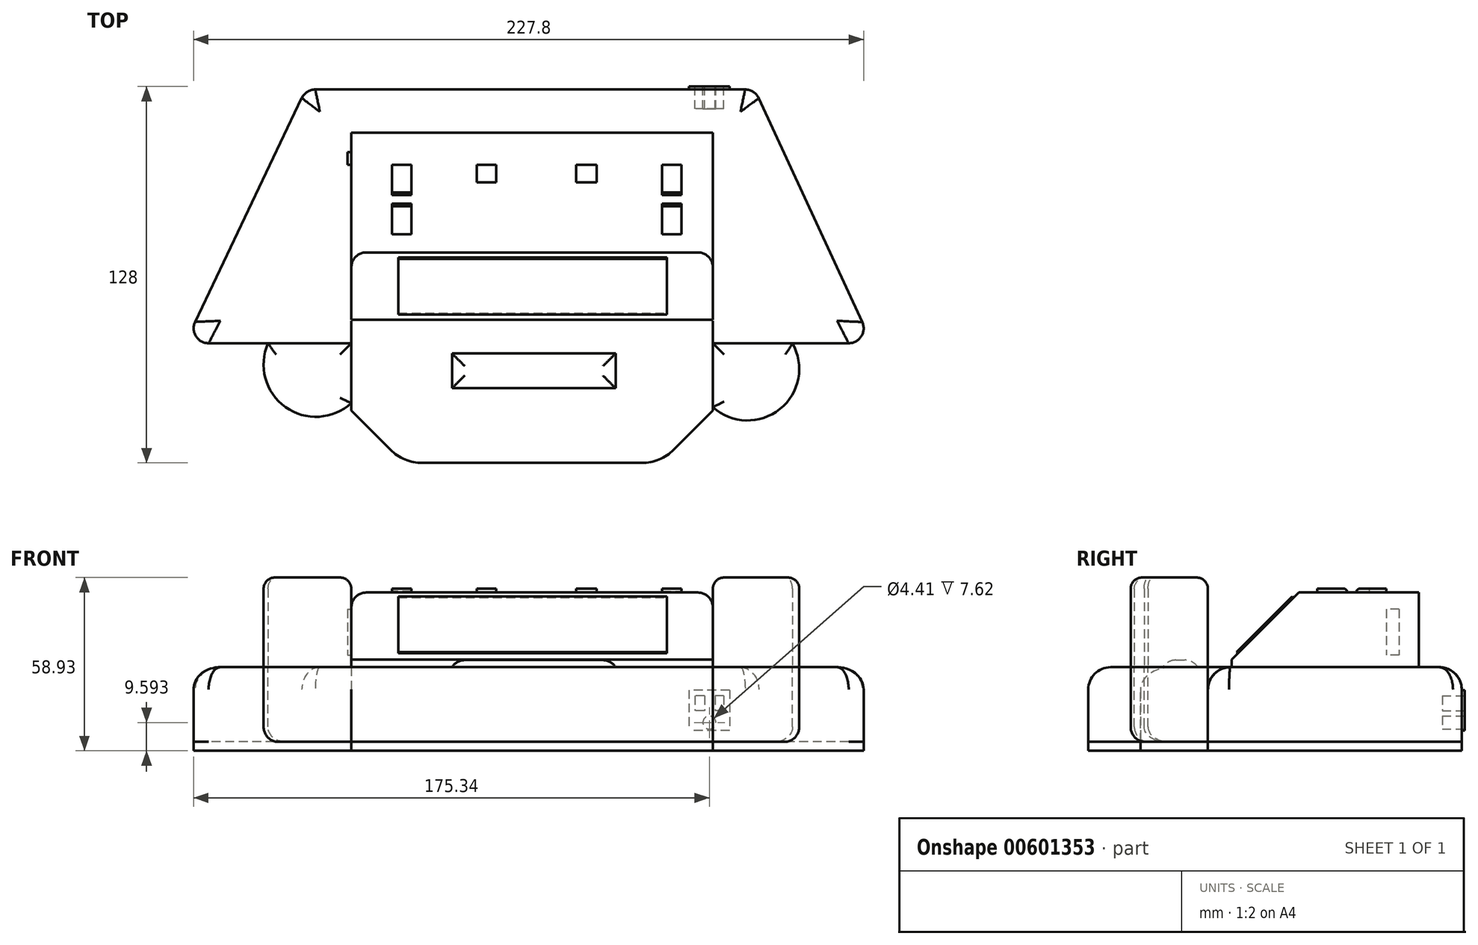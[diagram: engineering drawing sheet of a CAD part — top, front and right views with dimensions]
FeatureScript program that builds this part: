
annotation { "Feature Type Name" : "Feature", "Feature Type Description" : "" }
export const myFeature = defineFeature(function(context is Context, id is Id, definition is map)
    precondition{}
    {
        {
            var Q0;
            Q0=qCreatedBy(makeId("Top.planeOp"),FACE);
            var sketch = newSketch(context, id + "F0", { "sketchPlane" : qUnion([Q0])});
            skLineSegment(sketch, "E0", {"start": v(-105.32, 66.3) * mm, "end": v(-146.43, -19.98) * mm});
            skLineSegment(sketch, "E1", {"start": v(-146.43, -19.98) * mm, "end": v(-89.85, -19.98) * mm});
            skLineSegment(sketch, "E2", {"start": v(-89.85, -19.98) * mm, "end": v(-89.85, -60.68) * mm});
            skLineSegment(sketch, "E3", {"start": v(-89.85, -60.68) * mm, "end": v(33.07, -60.68) * mm});
            skLineSegment(sketch, "E4", {"start": v(33.07, -60.68) * mm, "end": v(33.07, -19.98) * mm});
            skLineSegment(sketch, "E5", {"start": v(33.07, -19.98) * mm, "end": v(87.2, -19.98) * mm});
            skLineSegment(sketch, "E6", {"start": v(87.2, -19.98) * mm, "end": v(47.31, 66.3) * mm});
            skLineSegment(sketch, "E7", {"start": v(47.31, 66.3) * mm, "end": v(-105.32, 66.3) * mm});
            skSolve(sketch);
        }
        {
            var Q0;
            Q0 = qSketchRegion(id + "F0", true);
            extrude(context, id + "F1", {"entities" : qUnion([Q0]), "depth" : 25.4 * mm, "offsetDistance" : 25.4 * mm});
        }
        {
            var Q0;
            Q0=makeQuery(id+"F1.opExtrude","CAP_FACE",FACE,{"disambiguationData":[OSD([sQuery(id+"F0.wireOp",EDGE,"E0"),sQuery(id+"F0.wireOp",EDGE,"E1"),sQuery(id+"F0.wireOp",EDGE,"E2"),sQuery(id+"F0.wireOp",EDGE,"E3"),sQuery(id+"F0.wireOp",EDGE,"E4"),sQuery(id+"F0.wireOp",EDGE,"E5"),sQuery(id+"F0.wireOp",EDGE,"E6"),sQuery(id+"F0.wireOp",EDGE,"E7")])],"isStart":false});
            var sketch = newSketch(context, id + "F2", { "sketchPlane" : qUnion([Q0])});
            skArc(sketch, "E8", {"start": v(-118.14, -19.98) * mm, "mid": v(-112.27, -41.66) * mm, "end": v(-89.85, -40.33) * mm});
            skArc(sketch, "E9", {"start": v(33.07, -41.66) * mm, "mid": v(55.87, -42.39) * mm, "end": v(60.13, -19.98) * mm});
            skPoint(sketch, "E9.startSnap0", {"position": v(-112.27, -41.66) * mm});
            skSolve(sketch);
        }
        {
            var Q0;
            {var subQ0=sQuery(id+"F2.wireOp",EDGE,"E9");Q0=makeQuery(id+"F2.imprint","IMPRINT",FACE,{"disambiguationData":[TD([[makeQuery(id+"F2.imprint","IMPRINT",EDGE,{"derivedFrom":subQ0}),1.0]])]});}
            var Q1;
            {var subQ0=sQuery(id+"F2.wireOp",EDGE,"E8");Q1=makeQuery(id+"F2.imprint","IMPRINT",FACE,{"disambiguationData":[TD([[makeQuery(id+"F2.imprint","IMPRINT",EDGE,{"derivedFrom":subQ0}),1.0]])]});}
            extrude(context, id + "F3", {"entities" : qUnion([Q0, Q1]), "oppositeDirection" : true, "depth" : 25.4 * mm, "offsetDistance" : 25.4 * mm});
        }
        {
            var Q0;
            Q0=makeQuery(id+"F1.opExtrude","SWEPT_EDGE",EDGE,{"disambiguationData":[OSD([sQuery(id+"F0.wireOp",EDGE,"E2"),sQuery(id+"F0.wireOp",EDGE,"E3")])]});
            var Q1;
            Q1=makeQuery(id+"F1.opExtrude","SWEPT_EDGE",EDGE,{"disambiguationData":[OSD([sQuery(id+"F0.wireOp",EDGE,"E3"),sQuery(id+"F0.wireOp",EDGE,"E4")])]});
            chamfer(context, id + "F4", {"entities" : qUnion([Q0, Q1]), "width" : 17.78 * mm, "tangentPropagation" : true});
        }
        {
            var Q0;
            Q0=makeQuery(id+"F3.opExtrude","CAP_FACE",FACE,{"disambiguationData":[OSD([sQuery(id+"F0.wireOp",EDGE,"E1"),sQuery(id+"F0.wireOp",EDGE,"E2"),sQuery(id+"F2.wireOp",EDGE,"E8")])],"isStart":true});
            var Q1;
            Q1=makeQuery(id+"F3.opExtrude","CAP_FACE",FACE,{"disambiguationData":[OSD([sQuery(id+"F0.wireOp",EDGE,"E4"),sQuery(id+"F0.wireOp",EDGE,"E5"),sQuery(id+"F2.wireOp",EDGE,"E9")])],"isStart":true});
            extrude(context, id + "F5", {"entities" : qUnion([Q0, Q1]), "depth" : 30.48 * mm, "offsetDistance" : 25.4 * mm});
        }
        {
            var Q0;
            Q0=makeQuery(id+"F1.opExtrude","CAP_FACE",FACE,{"disambiguationData":[OSD([sQuery(id+"F0.wireOp",EDGE,"E0"),sQuery(id+"F0.wireOp",EDGE,"E1"),sQuery(id+"F0.wireOp",EDGE,"E2"),sQuery(id+"F0.wireOp",EDGE,"E3"),sQuery(id+"F0.wireOp",EDGE,"E4"),sQuery(id+"F0.wireOp",EDGE,"E5"),sQuery(id+"F0.wireOp",EDGE,"E6"),sQuery(id+"F0.wireOp",EDGE,"E7")])],"isStart":false});
            var sketch = newSketch(context, id + "F6", { "sketchPlane" : qUnion([Q0])});
            skLineSegment(sketch, "E10", {"start": v(-89.85, 51.66) * mm, "end": v(33.07, 51.66) * mm});
            skLineSegment(sketch, "E11", {"start": v(33.07, 51.66) * mm, "end": v(33.07, -11.94) * mm});
            skLineSegment(sketch, "E12", {"start": v(33.07, -11.94) * mm, "end": v(-89.85, -11.94) * mm});
            skLineSegment(sketch, "E13", {"start": v(-89.85, -11.94) * mm, "end": v(-89.85, 51.66) * mm});
            skSolve(sketch);
        }
        {
            var Q0;
            Q0 = qSketchRegion(id + "F6", true);
            extrude(context, id + "F7", {"entities" : qUnion([Q0]), "depth" : 25.4 * mm, "offsetDistance" : 25.4 * mm});
        }
        {
            var Q0;
            Q0=makeQuery(id+"F7.opExtrude","CAP_EDGE",EDGE,{"disambiguationData":[OSD([sQuery(id+"F6.wireOp",EDGE,"E12")])],"isStart":false});
            chamfer(context, id + "F8", {"entities" : qUnion([Q0]), "width" : 22.86 * mm, "tangentPropagation" : true});
        }
        {
            var Q0;
            Q0=makeQuery(id+"F1.opExtrude","SWEPT_EDGE",EDGE,{"disambiguationData":[OSD([sQuery(id+"F0.wireOp",EDGE,"E0"),sQuery(id+"F0.wireOp",EDGE,"E1")])]});
            var Q1;
            Q1=makeQuery(id+"F1.opExtrude","SWEPT_EDGE",EDGE,{"disambiguationData":[OSD([sQuery(id+"F0.wireOp",EDGE,"E5"),sQuery(id+"F0.wireOp",EDGE,"E6")])]});
            var Q2;
            Q2=makeQuery(id+"F1.opExtrude","SWEPT_EDGE",EDGE,{"disambiguationData":[OSD([sQuery(id+"F0.wireOp",EDGE,"E6"),sQuery(id+"F0.wireOp",EDGE,"E7")])]});
            var Q3;
            Q3=makeQuery(id+"F1.opExtrude","SWEPT_EDGE",EDGE,{"disambiguationData":[OSD([sQuery(id+"F0.wireOp",EDGE,"E0"),sQuery(id+"F0.wireOp",EDGE,"E7")])]});
            fillet(context, id + "F9", {"entities" : qUnion([Q0, Q1, Q2, Q3]), "radius" : 5.08 * mm, "tangentPropagation" : true, "allowEdgeOverflow" : false});
        }
        {
            var Q0;
            {var subQ0=sQuery(id+"F0.wireOp",EDGE,"E3");Q0=makeQuery(id+"F4.opChamfer","BLEND_EDGE",EDGE,{"blendedFrom":[makeQuery(id+"F1.opExtrude","SWEPT_EDGE",EDGE,{"disambiguationData":[OSD([sQuery(id+"F0.wireOp",EDGE,"E2"),subQ0])]}),makeQuery(id+"F1.opExtrude","SWEPT_FACE",FACE,{"disambiguationData":[OSD([subQ0])]})],"blendedInto":[makeQuery(id+"F1.opExtrude","SWEPT_FACE",FACE,{"disambiguationData":[OSD([subQ0])]})]});}
            var Q1;
            {var subQ0=sQuery(id+"F0.wireOp",EDGE,"E3");Q1=makeQuery(id+"F4.opChamfer","BLEND_EDGE",EDGE,{"blendedFrom":[makeQuery(id+"F1.opExtrude","SWEPT_EDGE",EDGE,{"disambiguationData":[OSD([subQ0,sQuery(id+"F0.wireOp",EDGE,"E4")])]}),makeQuery(id+"F1.opExtrude","SWEPT_FACE",FACE,{"disambiguationData":[OSD([subQ0])]})],"blendedInto":[makeQuery(id+"F1.opExtrude","SWEPT_FACE",FACE,{"disambiguationData":[OSD([subQ0])]})]});}
            fillet(context, id + "F10", {"entities" : qUnion([Q0, Q1]), "radius" : 15.24 * mm, "tangentPropagation" : true, "allowEdgeOverflow" : false});
        }
        {
            var Q0;
            Q0=makeQuery(id+"F5.opExtrude","CAP_EDGE",EDGE,{"disambiguationData":[OSD([sQuery(id+"F2.wireOp",EDGE,"E8")])],"isStart":false});
            var Q1;
            Q1=makeQuery(id+"F5.opExtrude","CAP_EDGE",EDGE,{"disambiguationData":[OSD([sQuery(id+"F2.wireOp",EDGE,"E9")])],"isStart":false});
            var Q2;
            Q2=makeQuery(id+"F5.opExtrude","CAP_EDGE",EDGE,{"disambiguationData":[OSD([sQuery(id+"F0.wireOp",EDGE,"E4")])],"isStart":false});
            var Q3;
            Q3=makeQuery(id+"F5.opExtrude","CAP_EDGE",EDGE,{"disambiguationData":[OSD([sQuery(id+"F0.wireOp",EDGE,"E5")])],"isStart":false});
            var Q4;
            Q4=makeQuery(id+"F5.opExtrude","CAP_EDGE",EDGE,{"disambiguationData":[OSD([sQuery(id+"F0.wireOp",EDGE,"E2")])],"isStart":false});
            var Q5;
            Q5=makeQuery(id+"F5.opExtrude","CAP_EDGE",EDGE,{"disambiguationData":[OSD([sQuery(id+"F0.wireOp",EDGE,"E1")])],"isStart":false});
            fillet(context, id + "F11", {"entities" : qUnion([Q0, Q1, Q2, Q3, Q4, Q5]), "radius" : 3.8 * mm, "tangentPropagation" : true, "allowEdgeOverflow" : false});
        }
        {
            var Q0;
            Q0=makeQuery(id+"F1.opExtrude","CAP_FACE",FACE,{"disambiguationData":[OSD([sQuery(id+"F0.wireOp",EDGE,"E0"),sQuery(id+"F0.wireOp",EDGE,"E1"),sQuery(id+"F0.wireOp",EDGE,"E2"),sQuery(id+"F0.wireOp",EDGE,"E3"),sQuery(id+"F0.wireOp",EDGE,"E4"),sQuery(id+"F0.wireOp",EDGE,"E5"),sQuery(id+"F0.wireOp",EDGE,"E6"),sQuery(id+"F0.wireOp",EDGE,"E7")])],"isStart":true});
            var sketch = newSketch(context, id + "F12", { "sketchPlane" : qUnion([Q0])});
            skSolve(sketch);
        }
        {
            var Q0;
            {var subQ5=sQuery(id+"F0.wireOp",EDGE,"E4");Q0=makeQuery(id+"F12.imprint","IMPRINT",FACE,{"disambiguationData":[TD([[makeQuery(id+"F12.imprint","IMPRINT",EDGE,{"derivedFrom":makeQuery(id+"F1.opExtrude","CAP_EDGE",EDGE,{"disambiguationData":[OSD([subQ5])],"isStart":true})}),-1.0]])]});}
            extrude(context, id + "F13", {"entities" : qUnion([Q0]), "depth" : 3.05 * mm, "offsetDistance" : 25.4 * mm});
        }
        {
            var Q0;
            Q0=makeQuery(id+"F3.opExtrude","CAP_EDGE",EDGE,{"disambiguationData":[OSD([sQuery(id+"F2.wireOp",EDGE,"E8")])],"isStart":false});
            var Q1;
            Q1=makeQuery(id+"F3.opExtrude","CAP_EDGE",EDGE,{"disambiguationData":[OSD([sQuery(id+"F2.wireOp",EDGE,"E9")])],"isStart":false});
            fillet(context, id + "F14", {"entities" : qUnion([Q0, Q1]), "radius" : 5.08 * mm, "tangentPropagation" : true, "allowEdgeOverflow" : false});
        }
        {
            var Q0;
            Q0=makeQuery(id+"F7.opExtrude","CAP_FACE",FACE,{"disambiguationData":[OSD([sQuery(id+"F6.wireOp",EDGE,"E10"),sQuery(id+"F6.wireOp",EDGE,"E11"),sQuery(id+"F6.wireOp",EDGE,"E12"),sQuery(id+"F6.wireOp",EDGE,"E13")])],"isStart":false});
            var sketch = newSketch(context, id + "F15", { "sketchPlane" : qUnion([Q0])});
            skLineSegment(sketch, "E14", {"start": v(-6.4, 40.73) * mm, "end": v(-6.4, 34.78) * mm});
            skLineSegment(sketch, "E15", {"start": v(-6.4, 34.78) * mm, "end": v(-13.37, 34.78) * mm});
            skLineSegment(sketch, "E16", {"start": v(-13.37, 34.78) * mm, "end": v(-13.37, 40.73) * mm});
            skLineSegment(sketch, "E17", {"start": v(-13.37, 40.73) * mm, "end": v(-6.4, 40.73) * mm});
            skLineSegment(sketch, "E18", {"start": v(-47.2, 40.73) * mm, "end": v(-47.2, 34.78) * mm});
            skLineSegment(sketch, "E19", {"start": v(-47.2, 34.78) * mm, "end": v(-40.64, 34.78) * mm});
            skLineSegment(sketch, "E20", {"start": v(-40.64, 34.78) * mm, "end": v(-40.64, 40.73) * mm});
            skLineSegment(sketch, "E21", {"start": v(-40.64, 40.73) * mm, "end": v(-47.2, 40.73) * mm});
            skLineSegment(sketch, "E22.bottom", {"start": v(-76.04, 40.73) * mm, "end": v(-69.41, 40.73) * mm});
            skLineSegment(sketch, "E22.top", {"start": v(-76.04, 30.36) * mm, "end": v(-69.41, 30.36) * mm});
            skLineSegment(sketch, "E22.left", {"start": v(-76.04, 40.73) * mm, "end": v(-76.04, 30.36) * mm});
            skLineSegment(sketch, "E22.right", {"start": v(-69.41, 40.73) * mm, "end": v(-69.41, 30.36) * mm});
            skLineSegment(sketch, "E23.bottom", {"start": v(-69.41, 27.49) * mm, "end": v(-76.04, 27.49) * mm});
            skLineSegment(sketch, "E23.top", {"start": v(-69.41, 17.12) * mm, "end": v(-76.04, 17.12) * mm});
            skLineSegment(sketch, "E23.left", {"start": v(-69.41, 27.49) * mm, "end": v(-69.41, 17.12) * mm});
            skLineSegment(sketch, "E23.right", {"start": v(-76.04, 27.49) * mm, "end": v(-76.04, 17.12) * mm});
            skLineSegment(sketch, "E24.bottom", {"start": v(15.8, 40.73) * mm, "end": v(22.43, 40.73) * mm});
            skLineSegment(sketch, "E24.top", {"start": v(15.8, 30.36) * mm, "end": v(22.43, 30.36) * mm});
            skLineSegment(sketch, "E24.left", {"start": v(15.8, 40.73) * mm, "end": v(15.8, 30.36) * mm});
            skLineSegment(sketch, "E24.right", {"start": v(22.43, 40.73) * mm, "end": v(22.43, 30.36) * mm});
            skLineSegment(sketch, "E25.bottom", {"start": v(15.8, 27.5) * mm, "end": v(22.43, 27.5) * mm});
            skLineSegment(sketch, "E25.top", {"start": v(15.8, 17.12) * mm, "end": v(22.43, 17.12) * mm});
            skLineSegment(sketch, "E25.left", {"start": v(15.8, 27.5) * mm, "end": v(15.8, 17.12) * mm});
            skLineSegment(sketch, "E25.right", {"start": v(22.43, 27.5) * mm, "end": v(22.43, 17.12) * mm});
            skSolve(sketch);
        }
        {
            var Q0;
            Q0 = qSketchRegion(id + "F15", true);
            extrude(context, id + "F16", {"entities" : qUnion([Q0]), "depth" : 1.27 * mm, "offsetDistance" : 25.4 * mm});
        }
        {
            var Q0;
            Q0=makeQuery(id+"F7.opExtrude","SWEPT_FACE",FACE,{"disambiguationData":[OSD([sQuery(id+"F6.wireOp",EDGE,"E13")])]});
            var sketch = newSketch(context, id + "F17", { "sketchPlane" : qUnion([Q0])});
            skLineSegment(sketch, "E26.bottom", {"start": v(-45.04, 45.13) * mm, "end": v(-40.65, 45.13) * mm});
            skLineSegment(sketch, "E26.top", {"start": v(-45.04, 29.48) * mm, "end": v(-40.65, 29.48) * mm});
            skLineSegment(sketch, "E26.left", {"start": v(-45.04, 45.13) * mm, "end": v(-45.04, 29.48) * mm});
            skLineSegment(sketch, "E26.right", {"start": v(-40.65, 45.13) * mm, "end": v(-40.65, 29.48) * mm});
            skSolve(sketch);
        }
        {
            var Q0;
            Q0 = qSketchRegion(id + "F17", true);
            extrude(context, id + "F18", {"entities" : qUnion([Q0]), "depth" : 1.27 * mm, "offsetDistance" : 25.4 * mm});
        }
        {
            var Q0;
            Q0=makeQuery(id+"F7.opExtrude","CAP_EDGE",EDGE,{"disambiguationData":[OSD([sQuery(id+"F6.wireOp",EDGE,"E13")])],"isStart":false});
            var Q1;
            Q1=makeQuery(id+"F7.opExtrude","CAP_EDGE",EDGE,{"disambiguationData":[OSD([sQuery(id+"F6.wireOp",EDGE,"E11")])],"isStart":false});
            fillet(context, id + "F19", {"entities" : qUnion([Q0, Q1]), "radius" : 5.08 * mm, "tangentPropagation" : true, "allowEdgeOverflow" : false});
        }
        {
            var Q0;
            Q0=makeQuery(id+"F1.opExtrude","SWEPT_FACE",FACE,{"disambiguationData":[OSD([sQuery(id+"F0.wireOp",EDGE,"E7")])]});
            var sketch = newSketch(context, id + "F20", { "sketchPlane" : qUnion([Q0])});
            skLineSegment(sketch, "E27.bottom", {"start": v(-38.79, 17.63) * mm, "end": v(-24.98, 17.63) * mm});
            skLineSegment(sketch, "E27.top", {"start": v(-38.79, 3.92) * mm, "end": v(-24.98, 3.92) * mm});
            skLineSegment(sketch, "E27.left", {"start": v(-38.79, 17.63) * mm, "end": v(-38.79, 3.92) * mm});
            skLineSegment(sketch, "E27.right", {"start": v(-24.98, 17.63) * mm, "end": v(-24.98, 3.92) * mm});
            skSolve(sketch);
        }
        {
            var Q0;
            Q0 = qSketchRegion(id + "F20", true);
            extrude(context, id + "F21", {"entities" : qUnion([Q0]), "operationType" : NewBodyOperationType.ADD, "depth" : 1.02 * mm, "offsetDistance" : 25.4 * mm});
        }
        {
            var Q0;
            Q0=makeQuery(id+"F8.opChamfer","BLEND_FACE",FACE,{"disambiguationData":[OSD([sQuery(id+"F6.wireOp",EDGE,"E12")])]});
            var sketch = newSketch(context, id + "F22", { "sketchPlane" : qUnion([Q0])});
            skLineSegment(sketch, "E28.bottom", {"start": v(-73.9, 41.15) * mm, "end": v(17.49, 41.15) * mm});
            skLineSegment(sketch, "E28.top", {"start": v(-73.9, 14.38) * mm, "end": v(17.49, 14.38) * mm});
            skLineSegment(sketch, "E28.left", {"start": v(-73.9, 41.15) * mm, "end": v(-73.9, 14.38) * mm});
            skLineSegment(sketch, "E28.right", {"start": v(17.49, 41.15) * mm, "end": v(17.49, 14.38) * mm});
            skSolve(sketch);
        }
        {
            var Q0;
            Q0 = qSketchRegion(id + "F22", true);
            extrude(context, id + "F23", {"entities" : qUnion([Q0]), "depth" : 0.64 * mm, "offsetDistance" : 25.4 * mm});
        }
        {
            var Q0;
            Q0=makeQuery(id+"F1.opExtrude","CAP_FACE",FACE,{"disambiguationData":[OSD([sQuery(id+"F0.wireOp",EDGE,"E0"),sQuery(id+"F0.wireOp",EDGE,"E1"),sQuery(id+"F0.wireOp",EDGE,"E2"),sQuery(id+"F0.wireOp",EDGE,"E3"),sQuery(id+"F0.wireOp",EDGE,"E4"),sQuery(id+"F0.wireOp",EDGE,"E5"),sQuery(id+"F0.wireOp",EDGE,"E6"),sQuery(id+"F0.wireOp",EDGE,"E7")])],"isStart":false});
            var sketch = newSketch(context, id + "F24", { "sketchPlane" : qUnion([Q0])});
            skLineSegment(sketch, "E29.bottom", {"start": v(-55.6, -23.46) * mm, "end": v(0, -23.46) * mm});
            skLineSegment(sketch, "E29.top", {"start": v(-55.6, -35.26) * mm, "end": v(0, -35.26) * mm});
            skLineSegment(sketch, "E29.left", {"start": v(-55.6, -23.46) * mm, "end": v(-55.6, -35.26) * mm});
            skLineSegment(sketch, "E29.right", {"start": v(0, -23.46) * mm, "end": v(0, -35.26) * mm});
            skSolve(sketch);
        }
        {
            var Q0;
            Q0 = qSketchRegion(id + "F24", true);
            extrude(context, id + "F25", {"entities" : qUnion([Q0]), "depth" : 2.41 * mm, "offsetDistance" : 25.4 * mm});
        }
        {
            var Q0;
            Q0=makeQuery(id+"F25.opExtrude","CAP_EDGE",EDGE,{"disambiguationData":[OSD([sQuery(id+"F24.wireOp",EDGE,"E29.top")])],"isStart":false});
            var Q1;
            Q1=makeQuery(id+"F25.opExtrude","CAP_EDGE",EDGE,{"disambiguationData":[OSD([sQuery(id+"F24.wireOp",EDGE,"E29.right")])],"isStart":false});
            var Q2;
            Q2=makeQuery(id+"F25.opExtrude","CAP_EDGE",EDGE,{"disambiguationData":[OSD([sQuery(id+"F24.wireOp",EDGE,"E29.bottom")])],"isStart":false});
            var Q3;
            Q3=makeQuery(id+"F25.opExtrude","CAP_EDGE",EDGE,{"disambiguationData":[OSD([sQuery(id+"F24.wireOp",EDGE,"E29.left")])],"isStart":false});
            fillet(context, id + "F26", {"entities" : qUnion([Q0, Q1, Q2, Q3]), "radius" : 5.08 * mm, "tangentPropagation" : true, "allowEdgeOverflow" : false});
        }
        {
            var Q0;
            Q0=makeQuery(id+"F16.opExtrude","CAP_EDGE",EDGE,{"disambiguationData":[OSD([sQuery(id+"F15.wireOp",EDGE,"E22.top")])],"isStart":false});
            var Q1;
            Q1=makeQuery(id+"F16.opExtrude","CAP_EDGE",EDGE,{"disambiguationData":[OSD([sQuery(id+"F15.wireOp",EDGE,"E23.bottom")])],"isStart":false});
            var Q2;
            Q2=makeQuery(id+"F16.opExtrude","CAP_EDGE",EDGE,{"disambiguationData":[OSD([sQuery(id+"F15.wireOp",EDGE,"E24.top")])],"isStart":false});
            var Q3;
            Q3=makeQuery(id+"F16.opExtrude","CAP_EDGE",EDGE,{"disambiguationData":[OSD([sQuery(id+"F15.wireOp",EDGE,"E25.bottom")])],"isStart":false});
            chamfer(context, id + "F27", {"entities" : qUnion([Q0, Q1, Q2, Q3]), "width" : 0.89 * mm, "tangentPropagation" : true});
        }
        {
            var Q0;
            Q0=makeQuery(id+"F21.opExtrude","CAP_FACE",FACE,{"disambiguationData":[OSD([sQuery(id+"F20.wireOp",EDGE,"E27.bottom"),sQuery(id+"F20.wireOp",EDGE,"E27.top"),sQuery(id+"F20.wireOp",EDGE,"E27.left"),sQuery(id+"F20.wireOp",EDGE,"E27.right")])],"isStart":false});
            var sketch = newSketch(context, id + "F28", { "sketchPlane" : qUnion([Q0])});
            skLineSegment(sketch, "E30.bottom", {"start": v(-36.8, 15.64) * mm, "end": v(-33.85, 15.64) * mm});
            skLineSegment(sketch, "E30.top", {"start": v(-36.8, 10.6) * mm, "end": v(-33.85, 10.6) * mm});
            skLineSegment(sketch, "E30.left", {"start": v(-36.8, 15.64) * mm, "end": v(-36.8, 10.6) * mm});
            skLineSegment(sketch, "E30.right", {"start": v(-33.85, 15.64) * mm, "end": v(-33.85, 10.6) * mm});
            skLineSegment(sketch, "E31.bottom", {"start": v(-30.24, 15.64) * mm, "end": v(-26.96, 15.64) * mm});
            skLineSegment(sketch, "E31.top", {"start": v(-30.24, 10.6) * mm, "end": v(-26.96, 10.6) * mm});
            skLineSegment(sketch, "E31.left", {"start": v(-30.24, 15.64) * mm, "end": v(-30.24, 10.6) * mm});
            skLineSegment(sketch, "E31.right", {"start": v(-26.96, 15.64) * mm, "end": v(-26.96, 10.6) * mm});
            skCircle(sketch, "E32", {"center": v(-31.88, 6.54) * mm, "radius": 2.2 * mm});
            skSolve(sketch);
        }
        {
            var Q0;
            Q0 = qSketchRegion(id + "F28", true);
            extrude(context, id + "F29", {"entities" : qUnion([Q0]), "operationType" : NewBodyOperationType.REMOVE, "oppositeDirection" : true, "depth" : 7.62 * mm, "offsetDistance" : 25.4 * mm});
        }
        {
            var Q0;
            {var subQ0=sQuery(id+"F0.wireOp",EDGE,"E3");var subQ1=sQuery(id+"F0.wireOp",EDGE,"E2");Q0=makeQuery(id+"F4.opChamfer","BLEND_EDGE",EDGE,{"blendedFrom":[makeQuery(id+"F1.opExtrude","SWEPT_EDGE",EDGE,{"disambiguationData":[OSD([subQ1,subQ0])]}),makeQuery(id+"F1.opExtrude","CAP_FACE",FACE,{"disambiguationData":[OSD([sQuery(id+"F0.wireOp",EDGE,"E0"),sQuery(id+"F0.wireOp",EDGE,"E1"),subQ1,subQ0,sQuery(id+"F0.wireOp",EDGE,"E4"),sQuery(id+"F0.wireOp",EDGE,"E5"),sQuery(id+"F0.wireOp",EDGE,"E6"),sQuery(id+"F0.wireOp",EDGE,"E7")])],"isStart":false})],"blendedInto":[makeQuery(id+"F1.opExtrude","CAP_FACE",FACE,{"disambiguationData":[OSD([sQuery(id+"F0.wireOp",EDGE,"E0"),sQuery(id+"F0.wireOp",EDGE,"E1"),subQ1,subQ0,sQuery(id+"F0.wireOp",EDGE,"E4"),sQuery(id+"F0.wireOp",EDGE,"E5"),sQuery(id+"F0.wireOp",EDGE,"E6"),sQuery(id+"F0.wireOp",EDGE,"E7")])],"isStart":false})]});}
            var Q1;
            Q1=makeQuery(id+"F1.opExtrude","CAP_EDGE",EDGE,{"disambiguationData":[OSD([sQuery(id+"F0.wireOp",EDGE,"E1")])],"isStart":false});
            fillet(context, id + "F30", {"entities" : qUnion([Q0, Q1]), "radius" : 7.62 * mm, "tangentPropagation" : true, "allowEdgeOverflow" : false});
        }
    });
